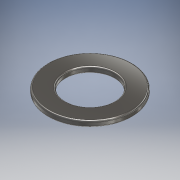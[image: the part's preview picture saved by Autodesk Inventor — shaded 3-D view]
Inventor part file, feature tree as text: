
AUTODESK INVENTOR PART (.ipt)
format: ipt  version: 2017 (Build 210142000, 142)  size: 137,728 bytes
history: native  units: mm
features: extrude x1, fillet x1, sketch x1
ambient origin geometry x8: Origin, YZ Plane, XZ Plane, XY Plane, X Axis, Y Axis, Z Axis, Center Point
bodies: Solid1 (feature_tree)
feature tree (3):
  extrude  "Extrusion1"  Depth=0.5mm
  fillet  "Fillet1"  Radius=2.0mm
  sketch  "Sketch1"  dims[d0=29.0mm d1=16.8mm d2=2.0mm d3=0.0mm d4=0.5mm]
